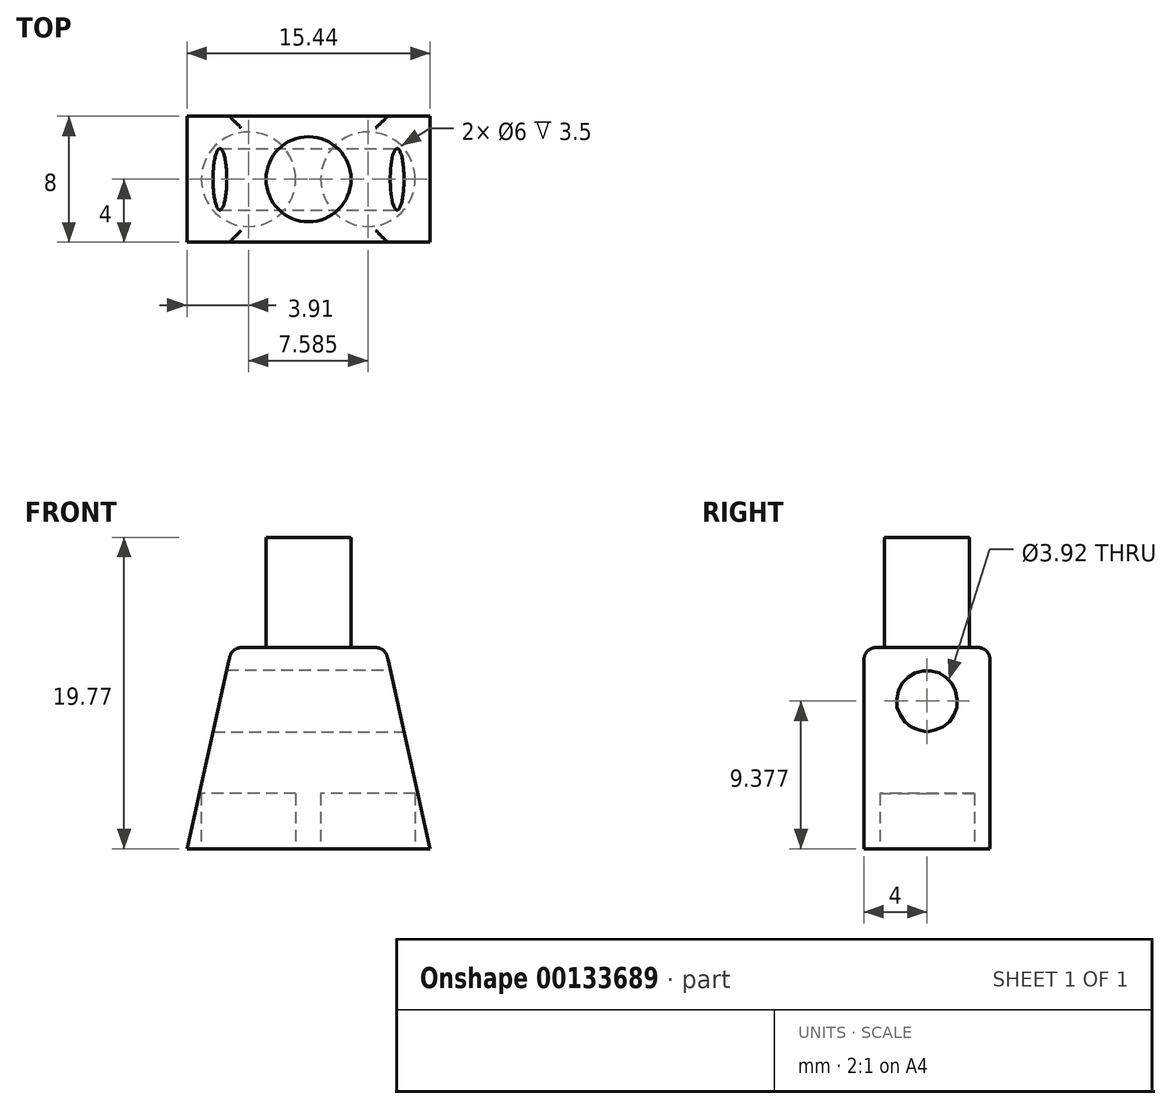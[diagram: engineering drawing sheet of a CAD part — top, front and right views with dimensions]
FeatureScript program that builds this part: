
annotation { "Feature Type Name" : "Feature", "Feature Type Description" : "" }
export const myFeature = defineFeature(function(context is Context, id is Id, definition is map)
    precondition{}
    {
        {
            var Q0;
            Q0=qCreatedBy(makeId("Top.planeOp"),FACE);
            var sketch = newSketch(context, id + "F0", { "sketchPlane" : qUnion([Q0])});
            skLineSegment(sketch, "E0.bottom", {"start": v(7.72, -4) * mm, "end": v(-7.72, -4) * mm});
            skLineSegment(sketch, "E0.top", {"start": v(7.72, 4) * mm, "end": v(-7.72, 4) * mm});
            skLineSegment(sketch, "E0.left", {"start": v(7.72, -4) * mm, "end": v(7.72, 4) * mm});
            skLineSegment(sketch, "E0.right", {"start": v(-7.72, -4) * mm, "end": v(-7.72, 4) * mm});
            skPoint(sketch, "E0.middle", {"position": v(0, 0) * mm});
            skSolve(sketch);
        }
        {
            var Q0;
            Q0=makeQuery(id+"F0.imprint","IMPRINT",FACE,{"disambiguationData":[TD([[makeQuery(id+"F0.imprint","IMPRINT",EDGE,{"derivedFrom":sQuery(id+"F0.wireOp",EDGE,"E0.bottom")}),-1.0]])]});
            cPlane(context, id + "F1", {"entities" : qUnion([Q0]), "cplaneType" : CPlaneType.OFFSET, "offset" : 12.77 * mm, "width" : 150 * mm, "height" : 150 * mm});
        }
        {
            var Q0;
            Q0=qCreatedBy(id+"F1.planeOp",FACE);
            var sketch = newSketch(context, id + "F2", { "sketchPlane" : qUnion([Q0])});
            skLineSegment(sketch, "E1.bottom", {"start": v(4.87, -4) * mm, "end": v(-4.87, -4) * mm});
            skLineSegment(sketch, "E1.top", {"start": v(4.87, 4) * mm, "end": v(-4.87, 4) * mm});
            skLineSegment(sketch, "E1.left", {"start": v(4.87, -4) * mm, "end": v(4.87, 4) * mm});
            skLineSegment(sketch, "E1.right", {"start": v(-4.87, -4) * mm, "end": v(-4.87, 4) * mm});
            skPoint(sketch, "E1.middle", {"position": v(0, 0) * mm});
            skSolve(sketch);
        }
        {
            var Q0;
            Q0=makeQuery(id+"F0.imprint","IMPRINT",FACE,{"disambiguationData":[TD([[makeQuery(id+"F0.imprint","IMPRINT",EDGE,{"derivedFrom":sQuery(id+"F0.wireOp",EDGE,"E0.bottom")}),-1.0]])]});
            var Q1;
            Q1=makeQuery(id+"F2.imprint","IMPRINT",FACE,{"disambiguationData":[TD([[makeQuery(id+"F2.imprint","IMPRINT",EDGE,{"derivedFrom":sQuery(id+"F2.wireOp",EDGE,"E1.bottom")}),-1.0]])]});
            loft(context, id + "F3", {"sheetProfilesArray" : [{ "sheetProfileEntities" : qUnion([Q0]) }, { "sheetProfileEntities" : qUnion([Q1]) }]});
        }
        {
            var Q0;
            Q0=makeQuery(id+"F3.opLoft","MID_CAP_EDGE",EDGE,{"disambiguationData":[OSD([sQuery(id+"F2.wireOp",EDGE,"E1.bottom"),sQuery(id+"F2.wireOp",EDGE,"E1.top"),sQuery(id+"F2.wireOp",EDGE,"E1.left")])],"capPos":1.0});
            var Q1;
            Q1=makeQuery(id+"F3.opLoft","MID_CAP_EDGE",EDGE,{"disambiguationData":[OSD([sQuery(id+"F2.wireOp",EDGE,"E1.bottom"),sQuery(id+"F2.wireOp",EDGE,"E1.left"),sQuery(id+"F2.wireOp",EDGE,"E1.right")])],"capPos":1.0});
            var Q2;
            Q2=makeQuery(id+"F3.opLoft","MID_CAP_EDGE",EDGE,{"disambiguationData":[OSD([sQuery(id+"F2.wireOp",EDGE,"E1.bottom"),sQuery(id+"F2.wireOp",EDGE,"E1.top"),sQuery(id+"F2.wireOp",EDGE,"E1.right")])],"capPos":1.0});
            var Q3;
            Q3=makeQuery(id+"F3.opLoft","MID_CAP_EDGE",EDGE,{"disambiguationData":[OSD([sQuery(id+"F2.wireOp",EDGE,"E1.top"),sQuery(id+"F2.wireOp",EDGE,"E1.left"),sQuery(id+"F2.wireOp",EDGE,"E1.right")])],"capPos":1.0});
            fillet(context, id + "F4", {"entities" : qUnion([Q0, Q1, Q2, Q3]), "radius" : 0.75 * mm, "tangentPropagation" : true, "allowEdgeOverflow" : false});
        }
        {
            var Q0;
            Q0=qCreatedBy(makeId("Right.planeOp"),FACE);
            cPlane(context, id + "F5", {"entities" : qUnion([Q0]), "cplaneType" : CPlaneType.OFFSET, "offset" : 25 * mm, "width" : 150 * mm, "height" : 150 * mm});
        }
        {
            var Q0;
            Q0=qCreatedBy(id+"F5.planeOp",FACE);
            var sketch = newSketch(context, id + "F6", { "sketchPlane" : qUnion([Q0])});
            skCircle(sketch, "E2", {"center": v(0, 9.38) * mm, "radius": 1.96 * mm});
            skLineSegment(sketch, "E3", {"start": v(0, 9.38) * mm, "end": v(0, 7.42) * mm});
            skSolve(sketch);
        }
        {
            var Q0;
            Q0=qSketchRegion(id+"F6",true);
            extrude(context, id + "F7", {"entities" : qUnion([Q0]), "operationType" : NewBodyOperationType.REMOVE, "oppositeDirection" : true, "depth" : 100 * mm});
        }
        {
            var Q0;
            Q0=qCreatedBy(makeId("Top.planeOp"),FACE);
            var sketch = newSketch(context, id + "F8", { "sketchPlane" : qUnion([Q0])});
            skPoint(sketch, "E4", {"position": v(3.78, 0) * mm});
            skPoint(sketch, "E5", {"position": v(-3.8, 0) * mm});
            skCircle(sketch, "E6", {"center": v(-3.8, 0) * mm, "radius": 3 * mm});
            skCircle(sketch, "E7", {"center": v(3.78, 0) * mm, "radius": 3 * mm});
            skSolve(sketch);
        }
        {
            var Q0;
            Q0=qSketchRegion(id+"F8",true);
            extrude(context, id + "F9", {"entities" : qUnion([Q0]), "operationType" : NewBodyOperationType.REMOVE, "depth" : 3.5 * mm});
        }
        {
            var Q0;
            Q0=qCreatedBy(id+"F1.planeOp",FACE);
            var sketch = newSketch(context, id + "F10", { "sketchPlane" : qUnion([Q0])});
            skCircle(sketch, "E8", {"center": v(0, 0) * mm, "radius": 2.7 * mm});
            skLineSegment(sketch, "E9", {"start": v(0, 0) * mm, "end": v(0, 2.7) * mm});
            skSolve(sketch);
        }
        {
            var Q0;
            Q0=qSketchRegion(id+"F10",true);
            extrude(context, id + "F11", {"entities" : qUnion([Q0]), "operationType" : NewBodyOperationType.ADD, "depth" : 7 * mm});
        }
    });
